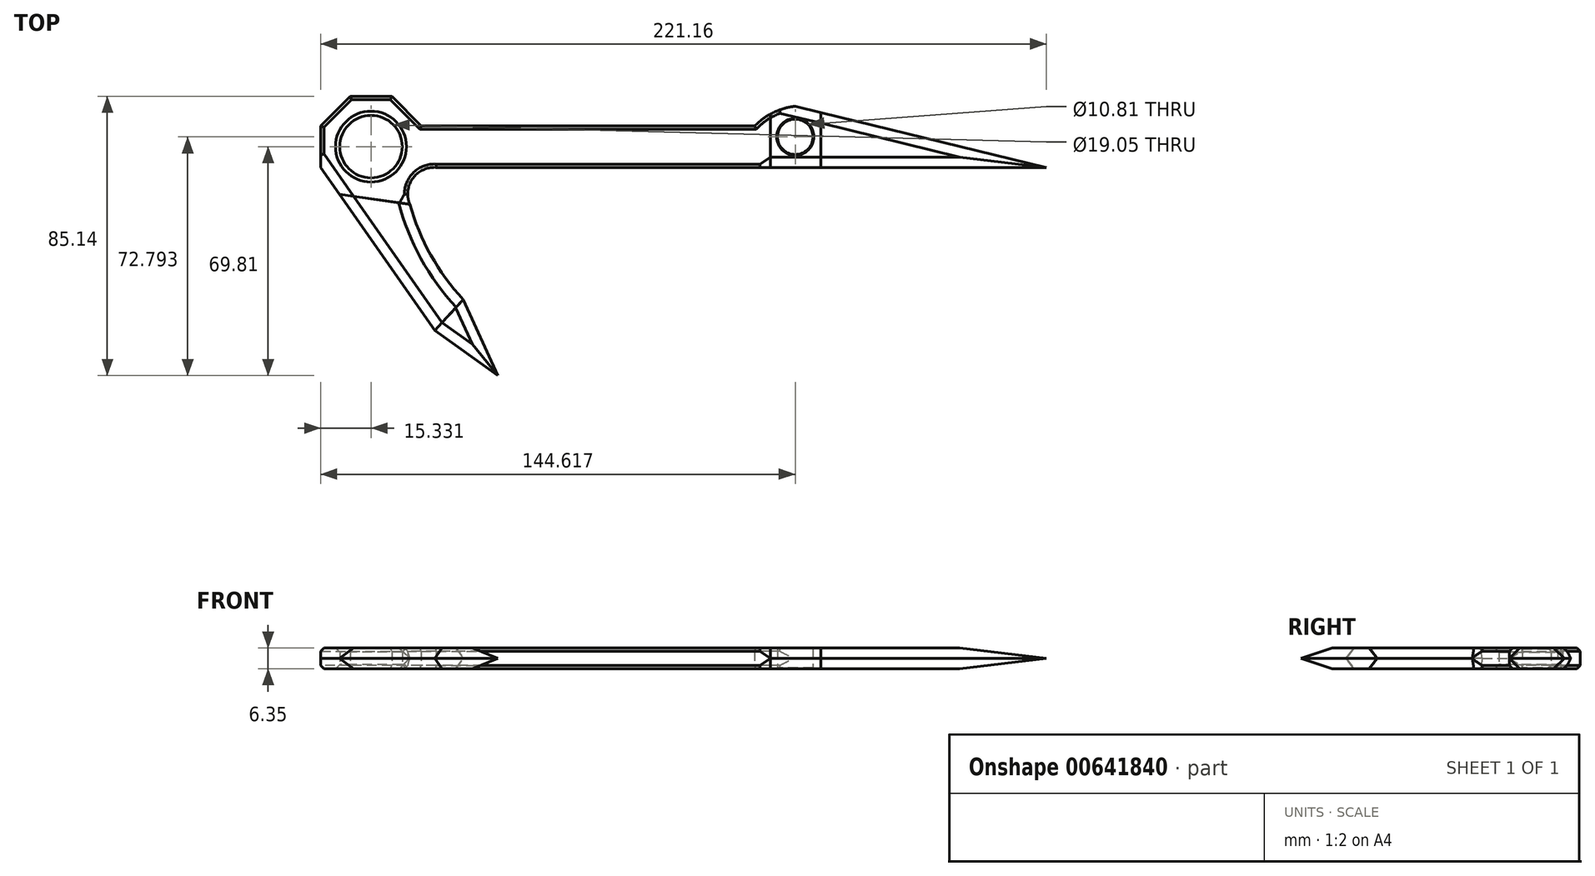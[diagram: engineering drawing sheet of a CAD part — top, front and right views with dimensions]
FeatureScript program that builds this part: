
annotation { "Feature Type Name" : "Feature", "Feature Type Description" : "" }
export const myFeature = defineFeature(function(context is Context, id is Id, definition is map)
    precondition{}
    {
        {
            var Q0;
            Q0=qCreatedBy(makeId("Top.planeOp"),FACE);
            var sketch = newSketch(context, id + "F0", { "sketchPlane" : qUnion([Q0])});
            skPoint(sketch, "E0.middle", {"position": v(0, 0) * mm});
            skLineSegment(sketch, "E1", {"start": v(-86.84, 44.45) * mm, "end": v(-95.82, 35.47) * mm});
            skLineSegment(sketch, "E2", {"start": v(-95.82, 35.47) * mm, "end": v(-95.82, 22.77) * mm});
            skLineSegment(sketch, "E3", {"start": v(-86.84, 44.45) * mm, "end": v(-74.14, 44.45) * mm});
            skLineSegment(sketch, "E4.MirrorCS", {"start": v(-74.14, 44.45) * mm, "end": v(-65.16, 35.47) * mm});
            skLineSegment(sketch, "E5", {"start": v(-65.16, 35.47) * mm, "end": v(36.44, 35.47) * mm});
            skLineSegment(sketch, "E6", {"start": v(-95.82, 22.77) * mm, "end": v(-61.02, -26.93) * mm});
            skLineSegment(sketch, "E7", {"start": v(-61.02, -26.93) * mm, "end": v(-41.8, -40.69) * mm});
            skLineSegment(sketch, "E8", {"start": v(-41.8, -40.69) * mm, "end": v(-52.39, -17.5) * mm});
            skArc(sketch, "E9", {"start": v(-68.64, 11.53) * mm, "mid": v(-62.24, -3.96) * mm, "end": v(-52.39, -17.5) * mm});
            skArc(sketch, "E10", {"start": v(-60.7, 22.77) * mm, "mid": v(-67.8, 19.37) * mm, "end": v(-68.64, 11.53) * mm});
            skLineSegment(sketch, "E11", {"start": v(-60.7, 22.77) * mm, "end": v(36.44, 22.77) * mm});
            skCircle(sketch, "E12", {"center": v(-80.49, 29.12) * mm, "radius": 9.53 * mm});
            skLineSegment(sketch, "E13", {"start": v(36.44, 22.77) * mm, "end": v(125.34, 22.77) * mm});
            skArc(sketch, "E14", {"start": v(48.8, 41.44) * mm, "mid": v(42.11, 39.5) * mm, "end": v(36.44, 35.47) * mm});
            skLineSegment(sketch, "E15", {"start": v(48.8, 41.44) * mm, "end": v(125.34, 22.77) * mm});
            skCircle(sketch, "E16", {"center": v(48.8, 32.1) * mm, "radius": 5.4 * mm});
            skLineSegment(sketch, "E17", {"start": v(56.6, 22.77) * mm, "end": v(56.6, 39.53) * mm});
            skLineSegment(sketch, "E18", {"start": v(-61.02, -26.93) * mm, "end": v(-52.39, -17.5) * mm});
            skLineSegment(sketch, "E19", {"start": v(-90.07, 14.57) * mm, "end": v(-68.64, 11.53) * mm});
            skLineSegment(sketch, "E20", {"start": v(41.23, 22.77) * mm, "end": v(41.23, 39.05) * mm});
            skSolve(sketch);
        }
        {
            var Q0;
            Q0=makeQuery(id+"F0.imprint","IMPRINT",FACE,{"disambiguationData":[TD([[makeQuery(id+"F0.imprint","IMPRINT",EDGE,{"derivedFrom":sQuery(id+"F0.wireOp",EDGE,"E1")}),1.0]])]});
            extrude(context, id + "F1", {"entities" : qUnion([Q0]), "depth" : 6.35 * mm, "offsetDistance" : 25.4 * mm});
        }
        {
            var Q0;
            Q0=makeQuery(id+"F0.imprint","IMPRINT",FACE,{"disambiguationData":[TD([[makeQuery(id+"F0.imprint","IMPRINT",EDGE,{"derivedFrom":sQuery(id+"F0.wireOp",EDGE,"E9")}),-1.0]])]});
            extrude(context, id + "F2", {"entities" : qUnion([Q0]), "depth" : 6.35 * mm, "offsetDistance" : 25.4 * mm});
        }
        {
            var Q0;
            Q0=makeQuery(id+"F0.imprint","IMPRINT",FACE,{"disambiguationData":[TD([[makeQuery(id+"F0.imprint","IMPRINT",EDGE,{"derivedFrom":sQuery(id+"F0.wireOp",EDGE,"E7")}),1.0]])]});
            extrude(context, id + "F3", {"entities" : qUnion([Q0]), "depth" : 6.35 * mm, "offsetDistance" : 25.4 * mm});
        }
        {
            var Q0;
            {var subQ3=sQuery(id+"F0.wireOp",EDGE,"E17");Q0=makeQuery(id+"F0.imprint","IMPRINT",FACE,{"disambiguationData":[TD([[makeQuery(id+"F0.imprint","IMPRINT",EDGE,{"derivedFrom":subQ3}),-1.0]])]});}
            extrude(context, id + "F4", {"entities" : qUnion([Q0]), "depth" : 6.35 * mm, "offsetDistance" : 25.4 * mm});
        }
        {
            var Q0;
            Q0=makeQuery(id+"F4.opExtrude","CAP_EDGE",EDGE,{"disambiguationData":[OSD([sQuery(id+"F0.wireOp",EDGE,"E15")])],"isStart":false});
            var Q1;
            Q1=makeQuery(id+"F4.opExtrude","CAP_EDGE",EDGE,{"disambiguationData":[OSD([sQuery(id+"F0.wireOp",EDGE,"E13")])],"isStart":false});
            var Q2;
            Q2=makeQuery(id+"F4.opExtrude","CAP_EDGE",EDGE,{"disambiguationData":[OSD([sQuery(id+"F0.wireOp",EDGE,"E15")])],"isStart":true});
            var Q3;
            Q3=makeQuery(id+"F4.opExtrude","CAP_EDGE",EDGE,{"disambiguationData":[OSD([sQuery(id+"F0.wireOp",EDGE,"E13")])],"isStart":true});
            chamfer(context, id + "F5", {"entities" : qUnion([Q0, Q1, Q2, Q3]), "chamferType" : ChamferType.TWO_OFFSETS, "width1" : 3.17 * mm, "oppositeDirection" : false, "width2" : 3.17 * mm, "tangentPropagation" : true});
        }
        {
            var Q0;
            Q0=makeQuery(id+"F0.imprint","IMPRINT",FACE,{"disambiguationData":[TD([[makeQuery(id+"F0.imprint","IMPRINT",EDGE,{"derivedFrom":sQuery(id+"F0.wireOp",EDGE,"E16")}),-1.0]])]});
            extrude(context, id + "F6", {"entities" : qUnion([Q0]), "depth" : 6.35 * mm, "offsetDistance" : 25.4 * mm});
        }
        {
            var Q0;
            Q0=makeQuery(id+"F6.opExtrude","CAP_EDGE",EDGE,{"disambiguationData":[OSD([sQuery(id+"F0.wireOp",EDGE,"E15")])],"isStart":false});
            var Q1;
            Q1=makeQuery(id+"F6.opExtrude","CAP_EDGE",EDGE,{"disambiguationData":[OSD([sQuery(id+"F0.wireOp",EDGE,"E15")])],"isStart":true});
            var Q2;
            Q2=makeQuery(id+"F6.opExtrude","CAP_EDGE",EDGE,{"disambiguationData":[OSD([sQuery(id+"F0.wireOp",EDGE,"E13")])],"isStart":true});
            var Q3;
            Q3=makeQuery(id+"F6.opExtrude","CAP_EDGE",EDGE,{"disambiguationData":[OSD([sQuery(id+"F0.wireOp",EDGE,"E13")])],"isStart":false});
            chamfer(context, id + "F7", {"entities" : qUnion([Q0, Q1, Q2, Q3]), "chamferType" : ChamferType.TWO_OFFSETS, "width1" : 3.17 * mm, "oppositeDirection" : false, "width2" : 3.17 * mm, "tangentPropagation" : true});
        }
        {
            var Q0;
            Q0=makeQuery(id+"F3.opExtrude","CAP_EDGE",EDGE,{"disambiguationData":[OSD([sQuery(id+"F0.wireOp",EDGE,"E8")])],"isStart":false});
            var Q1;
            Q1=makeQuery(id+"F3.opExtrude","CAP_EDGE",EDGE,{"disambiguationData":[OSD([sQuery(id+"F0.wireOp",EDGE,"E7")])],"isStart":false});
            var Q2;
            Q2=makeQuery(id+"F3.opExtrude","CAP_EDGE",EDGE,{"disambiguationData":[OSD([sQuery(id+"F0.wireOp",EDGE,"E8")])],"isStart":true});
            var Q3;
            Q3=makeQuery(id+"F3.opExtrude","CAP_EDGE",EDGE,{"disambiguationData":[OSD([sQuery(id+"F0.wireOp",EDGE,"E7")])],"isStart":true});
            chamfer(context, id + "F8", {"entities" : qUnion([Q0, Q1, Q2, Q3]), "chamferType" : ChamferType.TWO_OFFSETS, "width1" : 3.17 * mm, "oppositeDirection" : false, "width2" : 3.17 * mm, "tangentPropagation" : true});
        }
        {
            var Q0;
            Q0=makeQuery(id+"F2.opExtrude","CAP_EDGE",EDGE,{"disambiguationData":[OSD([sQuery(id+"F0.wireOp",EDGE,"E9")])],"isStart":false});
            var Q1;
            Q1=makeQuery(id+"F2.opExtrude","CAP_EDGE",EDGE,{"disambiguationData":[OSD([sQuery(id+"F0.wireOp",EDGE,"E9")])],"isStart":true});
            var Q2;
            Q2=makeQuery(id+"F2.opExtrude","CAP_EDGE",EDGE,{"disambiguationData":[OSD([sQuery(id+"F0.wireOp",EDGE,"E6")])],"isStart":true});
            var Q3;
            Q3=makeQuery(id+"F2.opExtrude","CAP_EDGE",EDGE,{"disambiguationData":[OSD([sQuery(id+"F0.wireOp",EDGE,"E6")])],"isStart":false});
            chamfer(context, id + "F9", {"entities" : qUnion([Q0, Q1, Q2, Q3]), "chamferType" : ChamferType.TWO_OFFSETS, "width1" : 3.17 * mm, "oppositeDirection" : false, "width2" : 3.17 * mm, "tangentPropagation" : true});
        }
        {
            var Q0;
            Q0=makeQuery(id+"F1.opExtrude","CAP_EDGE",EDGE,{"disambiguationData":[OSD([sQuery(id+"F0.wireOp",EDGE,"E12")])],"isStart":false});
            var Q1;
            Q1=makeQuery(id+"F1.opExtrude","CAP_EDGE",EDGE,{"disambiguationData":[OSD([sQuery(id+"F0.wireOp",EDGE,"E12")])],"isStart":true});
            chamfer(context, id + "F10", {"entities" : qUnion([Q0, Q1]), "width" : 1.27 * mm, "tangentPropagation" : true});
        }
        {
            var Q0;
            Q0=makeQuery(id+"F1.opExtrude","CAP_EDGE",EDGE,{"disambiguationData":[OSD([sQuery(id+"F0.wireOp",EDGE,"E6")])],"isStart":false});
            var Q1;
            Q1=makeQuery(id+"F1.opExtrude","CAP_EDGE",EDGE,{"disambiguationData":[OSD([sQuery(id+"F0.wireOp",EDGE,"E6")])],"isStart":true});
            chamfer(context, id + "F11", {"entities" : qUnion([Q0, Q1]), "width" : 3.17 * mm, "tangentPropagation" : true});
        }
        {
            var Q0;
            Q0=makeQuery(id+"F6.opExtrude","CAP_EDGE",EDGE,{"disambiguationData":[OSD([sQuery(id+"F0.wireOp",EDGE,"E16")])],"isStart":true});
            var Q1;
            Q1=makeQuery(id+"F6.opExtrude","CAP_EDGE",EDGE,{"disambiguationData":[OSD([sQuery(id+"F0.wireOp",EDGE,"E16")])],"isStart":false});
            chamfer(context, id + "F12", {"entities" : qUnion([Q0, Q1]), "width" : 0.25 * mm, "tangentPropagation" : true});
        }
        {
            var Q0;
            Q0=makeQuery(id+"F1.opExtrude","CAP_EDGE",EDGE,{"disambiguationData":[OSD([sQuery(id+"F0.wireOp",EDGE,"E2")])],"isStart":false});
            var Q1;
            Q1=makeQuery(id+"F1.opExtrude","CAP_EDGE",EDGE,{"disambiguationData":[OSD([sQuery(id+"F0.wireOp",EDGE,"E2")])],"isStart":true});
            var Q2;
            Q2=makeQuery(id+"F1.opExtrude","CAP_EDGE",EDGE,{"disambiguationData":[OSD([sQuery(id+"F0.wireOp",EDGE,"E1")])],"isStart":true});
            var Q3;
            Q3=makeQuery(id+"F1.opExtrude","CAP_EDGE",EDGE,{"disambiguationData":[OSD([sQuery(id+"F0.wireOp",EDGE,"E1")])],"isStart":false});
            var Q4;
            Q4=makeQuery(id+"F1.opExtrude","CAP_EDGE",EDGE,{"disambiguationData":[OSD([sQuery(id+"F0.wireOp",EDGE,"E3")])],"isStart":false});
            var Q5;
            Q5=makeQuery(id+"F1.opExtrude","CAP_EDGE",EDGE,{"disambiguationData":[OSD([sQuery(id+"F0.wireOp",EDGE,"E3")])],"isStart":true});
            var Q6;
            Q6=makeQuery(id+"F1.opExtrude","CAP_EDGE",EDGE,{"disambiguationData":[OSD([sQuery(id+"F0.wireOp",EDGE,"E4.MirrorCS")])],"isStart":false});
            var Q7;
            Q7=makeQuery(id+"F1.opExtrude","CAP_EDGE",EDGE,{"disambiguationData":[OSD([sQuery(id+"F0.wireOp",EDGE,"E4.MirrorCS")])],"isStart":true});
            var Q8;
            Q8=makeQuery(id+"F1.opExtrude","CAP_EDGE",EDGE,{"disambiguationData":[OSD([sQuery(id+"F0.wireOp",EDGE,"E5")])],"isStart":false});
            var Q9;
            Q9=makeQuery(id+"F1.opExtrude","CAP_EDGE",EDGE,{"disambiguationData":[OSD([sQuery(id+"F0.wireOp",EDGE,"E5")])],"isStart":true});
            var Q10;
            Q10=makeQuery(id+"F1.opExtrude","CAP_EDGE",EDGE,{"disambiguationData":[OSD([sQuery(id+"F0.wireOp",EDGE,"E11"),sQuery(id+"F0.wireOp",EDGE,"E13")])],"isStart":true});
            var Q11;
            Q11=makeQuery(id+"F1.opExtrude","CAP_EDGE",EDGE,{"disambiguationData":[OSD([sQuery(id+"F0.wireOp",EDGE,"E11"),sQuery(id+"F0.wireOp",EDGE,"E13")])],"isStart":false});
            var Q12;
            Q12=makeQuery(id+"F1.opExtrude","CAP_EDGE",EDGE,{"disambiguationData":[OSD([sQuery(id+"F0.wireOp",EDGE,"E10")])],"isStart":true});
            var Q13;
            Q13=makeQuery(id+"F1.opExtrude","CAP_EDGE",EDGE,{"disambiguationData":[OSD([sQuery(id+"F0.wireOp",EDGE,"E10")])],"isStart":false});
            var Q14;
            Q14=makeQuery(id+"F1.opExtrude","CAP_EDGE",EDGE,{"disambiguationData":[OSD([sQuery(id+"F0.wireOp",EDGE,"E14")])],"isStart":false});
            var Q15;
            Q15=makeQuery(id+"F1.opExtrude","CAP_EDGE",EDGE,{"disambiguationData":[OSD([sQuery(id+"F0.wireOp",EDGE,"E14")])],"isStart":true});
            var Q16;
            Q16=makeQuery(id+"F6.opExtrude","CAP_EDGE",EDGE,{"disambiguationData":[OSD([sQuery(id+"F0.wireOp",EDGE,"E14")])],"isStart":false});
            var Q17;
            Q17=makeQuery(id+"F6.opExtrude","CAP_EDGE",EDGE,{"disambiguationData":[OSD([sQuery(id+"F0.wireOp",EDGE,"E14")])],"isStart":true});
            chamfer(context, id + "F13", {"entities" : qUnion([Q0, Q1, Q2, Q3, Q4, Q5, Q6, Q7, Q8, Q9, Q10, Q11, Q12, Q13, Q14, Q15, Q16, Q17]), "width" : 1.02 * mm, "tangentPropagation" : true});
        }
        {
            var Q0;
            Q0=makeQuery(id+"F13.opChamfer","BLEND_EDGE",EDGE,{"blendedFrom":[makeQuery(id+"F1.opExtrude","CAP_EDGE",EDGE,{"disambiguationData":[OSD([sQuery(id+"F0.wireOp",EDGE,"E11"),sQuery(id+"F0.wireOp",EDGE,"E13")])],"isStart":false}),makeQuery(id+"F1.opExtrude","SWEPT_FACE",FACE,{"disambiguationData":[OSD([sQuery(id+"F0.wireOp",EDGE,"E20")])]})],"blendedInto":[makeQuery(id+"F1.opExtrude","SWEPT_FACE",FACE,{"disambiguationData":[OSD([sQuery(id+"F0.wireOp",EDGE,"E20")])]})]});
            var Q1;
            Q1=makeQuery(id+"F13.opChamfer","BLEND_EDGE",EDGE,{"blendedFrom":[makeQuery(id+"F1.opExtrude","CAP_EDGE",EDGE,{"disambiguationData":[OSD([sQuery(id+"F0.wireOp",EDGE,"E11"),sQuery(id+"F0.wireOp",EDGE,"E13")])],"isStart":true}),makeQuery(id+"F1.opExtrude","SWEPT_FACE",FACE,{"disambiguationData":[OSD([sQuery(id+"F0.wireOp",EDGE,"E20")])]})],"blendedInto":[makeQuery(id+"F1.opExtrude","SWEPT_FACE",FACE,{"disambiguationData":[OSD([sQuery(id+"F0.wireOp",EDGE,"E20")])]})]});
            chamfer(context, id + "F14", {"entities" : qUnion([Q0, Q1]), "chamferType" : ChamferType.TWO_OFFSETS, "width1" : 1.52 * mm, "oppositeDirection" : false, "width2" : 3.17 * mm, "tangentPropagation" : true});
        }
        {
            var Q0;
            Q0=makeQuery(id+"F13.opChamfer","BLEND_EDGE",EDGE,{"blendedFrom":[makeQuery(id+"F1.opExtrude","CAP_EDGE",EDGE,{"disambiguationData":[OSD([sQuery(id+"F0.wireOp",EDGE,"E10")])],"isStart":true}),makeQuery(id+"F1.opExtrude","SWEPT_FACE",FACE,{"disambiguationData":[OSD([sQuery(id+"F0.wireOp",EDGE,"E19")])]})],"blendedInto":[makeQuery(id+"F1.opExtrude","SWEPT_FACE",FACE,{"disambiguationData":[OSD([sQuery(id+"F0.wireOp",EDGE,"E19")])]})]});
            var Q1;
            Q1=makeQuery(id+"F13.opChamfer","BLEND_EDGE",EDGE,{"blendedFrom":[makeQuery(id+"F1.opExtrude","CAP_EDGE",EDGE,{"disambiguationData":[OSD([sQuery(id+"F0.wireOp",EDGE,"E10")])],"isStart":false}),makeQuery(id+"F1.opExtrude","SWEPT_FACE",FACE,{"disambiguationData":[OSD([sQuery(id+"F0.wireOp",EDGE,"E19")])]})],"blendedInto":[makeQuery(id+"F1.opExtrude","SWEPT_FACE",FACE,{"disambiguationData":[OSD([sQuery(id+"F0.wireOp",EDGE,"E19")])]})]});
            chamfer(context, id + "F15", {"entities" : qUnion([Q0, Q1]), "chamferType" : ChamferType.TWO_OFFSETS, "width1" : 1.78 * mm, "oppositeDirection" : false, "width2" : 3.17 * mm, "tangentPropagation" : true});
        }
    });
